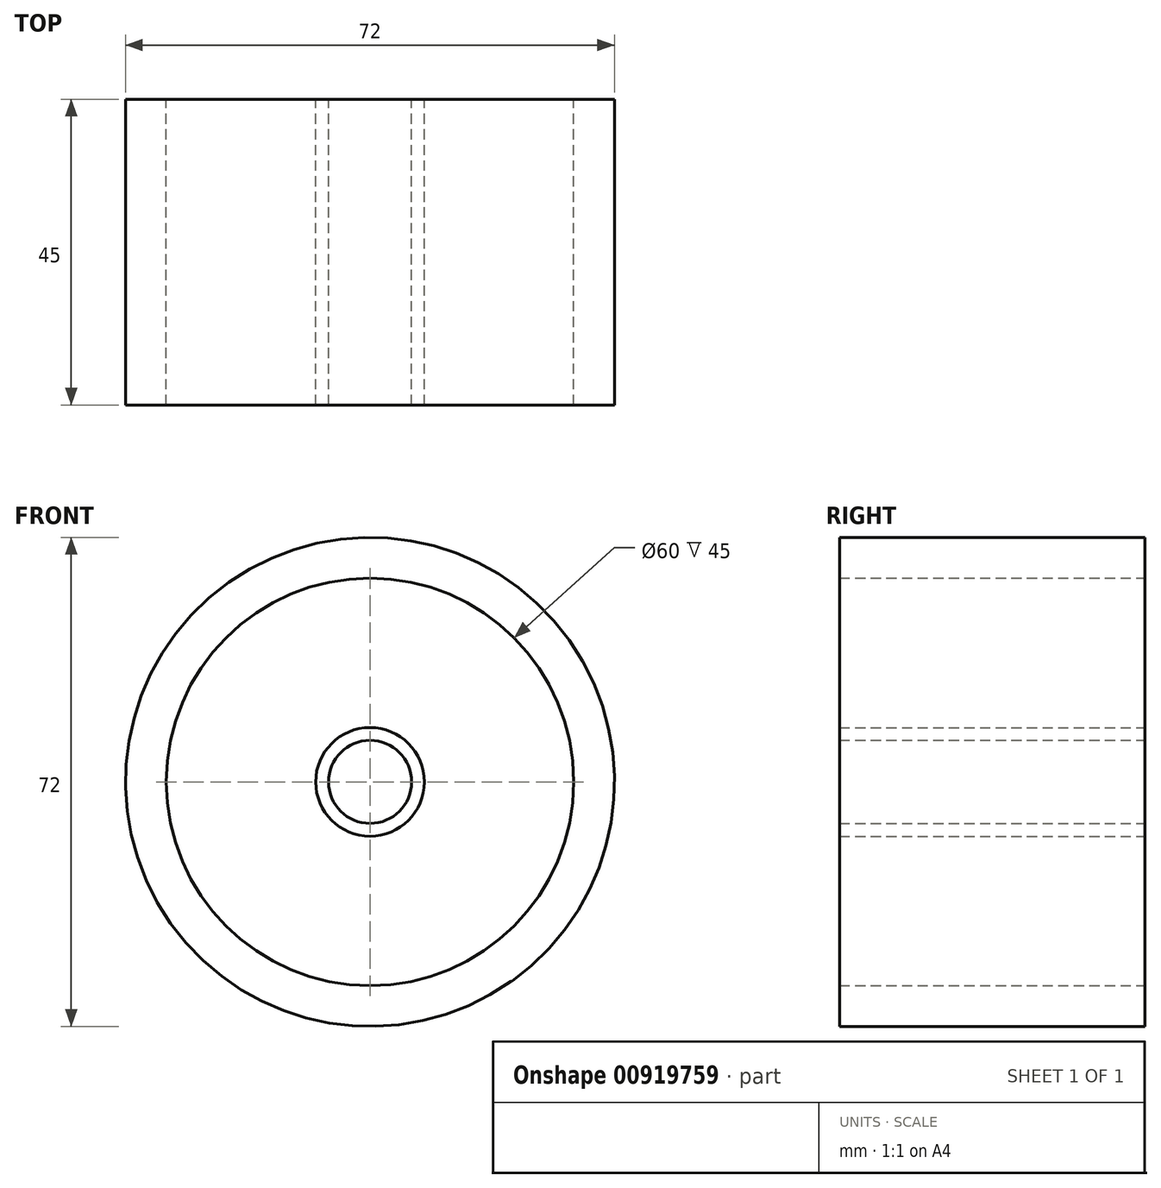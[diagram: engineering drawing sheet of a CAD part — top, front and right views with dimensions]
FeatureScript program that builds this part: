
annotation { "Feature Type Name" : "Feature", "Feature Type Description" : "" }
export const myFeature = defineFeature(function(context is Context, id is Id, definition is map)
    precondition{}
    {
        {
            var Q0;
            Q0=qCreatedBy(makeId("Front.planeOp"),FACE);
            var sketch = newSketch(context, id + "F0", { "sketchPlane" : qUnion([Q0])});
            skCircle(sketch, "E0", {"center": v(0, 0) * mm, "radius": 8 * mm});
            skLineSegment(sketch, "E1.0", {"start": v(-335.4, -14.59) * mm, "end": v(-335.4, -164.59) * mm});
            skCircle(sketch, "E2.0", {"center": v(0, 0) * mm, "radius": 6.12 * mm});
            skCircle(sketch, "E3", {"center": v(0, 0) * mm, "radius": 30 * mm});
            skCircle(sketch, "E4.0", {"center": v(0, 0) * mm, "radius": 36 * mm});
            skFitSpline(sketch, "E5", {"points": [v(-752.9, -15.16) * mm, v(-700, -10.98) * mm, v(-659.23, -24.07) * mm, v(-335.4, -164.59) * mm, v(17.4, -24.44) * mm], "startDerivative": vector(415.77, 48.15) * mm, "endDerivative": vector(894.71, 636.72) * mm});
            skFitSpline(sketch, "E6.0", {"points": [v(-752.21, -21.12) * mm, v(-747.88, -20.62) * mm, v(-741.4, -19.87) * mm, v(-732.98, -18.95) * mm, v(-726.81, -18.34) * mm, v(-720.84, -17.8) * mm, v(-716.06, -17.45) * mm, v(-712.38, -17.23) * mm, v(-709.7, -17.1) * mm, v(-707.1, -17.01) * mm, v(-704.6, -16.96) * mm, v(-702.59, -16.95) * mm, v(-701.04, -16.96) * mm, v(-699.9, -16.99) * mm, v(-698.79, -17.02) * mm, v(-697.35, -17.08) * mm, v(-695.61, -17.19) * mm, v(-693.6, -17.38) * mm, v(-691, -17.71) * mm, v(-688.43, -18.2) * mm, v(-685.78, -18.86) * mm, v(-683.73, -19.47) * mm, v(-681.58, -20.19) * mm, v(-678.56, -21.31) * mm, v(-674.43, -23.07) * mm, v(-669.7, -25.36) * mm, v(-665.45, -27.54) * mm, v(-662.04, -29.37) * mm, v(-658.36, -31.39) * mm, v(-653.12, -34.33) * mm, v(-645.96, -38.44) * mm, v(-636.46, -43.99) * mm, v(-626.1, -50.09) * mm, v(-614.96, -56.65) * mm, v(-603.07, -63.6) * mm, v(-590.49, -70.88) * mm, v(-577.28, -78.4) * mm, v(-558.88, -88.66) * mm, v(-534.54, -101.72) * mm, v(-503.62, -117.2) * mm, v(-471.37, -131.9) * mm, v(-443.73, -143) * mm, v(-421.35, -150.9) * mm, v(-404.48, -156.27) * mm, v(-387.58, -161) * mm, v(-373.5, -164.34) * mm, v(-362.27, -166.62) * mm, v(-353.87, -168.12) * mm, v(-346.89, -169.2) * mm, v(-341.32, -169.94) * mm, v(-337.16, -170.44) * mm, v(-333, -170.88) * mm, v(-327.48, -171.4) * mm, v(-320.6, -171.88) * mm, v(-312.4, -172.24) * mm, v(-301.53, -172.42) * mm, v(-288.05, -172.1) * mm, v(-272.07, -170.86) * mm, v(-256.26, -168.82) * mm, v(-235.41, -165.09) * mm, v(-209.76, -158.6) * mm, v(-179.59, -148.25) * mm, v(-149.94, -135.62) * mm, v(-120.75, -121.03) * mm, v(-91.95, -104.8) * mm, v(-63.46, -87.21) * mm, v(-25.79, -62.36) * mm, v(2.22, -42.6) * mm, v(20.87, -29.33) * mm]});
            skLineSegment(sketch, "E7", {"start": v(-752.9, -15.16) * mm, "end": v(-752.21, -21.12) * mm});
            skSolve(sketch);
        }
        {
            var Q0;
            {var subQ0=sQuery(id+"F0.wireOp",EDGE,"E6.0");Q0=makeQuery(id+"F0.imprint","IMPRINT",FACE,{"disambiguationData":[TD([[makeQuery(id+"F0.imprint","IMPRINT",EDGE,{"derivedFrom":subQ0}),1.0]])]});}
            var Q1;
            {var subQ0=sQuery(id+"F0.wireOp",EDGE,"E3");var subQ1=makeQuery(id+"F0.imprint","IMPRINT",VERTEX,{"disambiguationData":[OD(0.0)],"derivedFrom":subQ0});Q1=makeQuery(id+"F0.imprint","IMPRINT",FACE,{"disambiguationData":[TD([[makeQuery(id+"F0.imprint","IMPRINT",EDGE,{"disambiguationData":[TD([[subQ1,-1.0]])],"derivedFrom":subQ0}),-1.0]])]});}
            var Q2;
            Q2=makeQuery(id+"F0.imprint","IMPRINT",FACE,{"disambiguationData":[TD([[makeQuery(id+"F0.imprint","IMPRINT",EDGE,{"derivedFrom":sQuery(id+"F0.wireOp",EDGE,"E0")}),1.0]])]});
            extrude(context, id + "F1", {"entities" : qUnion([Q0, Q1, Q2]), "depth" : 45 * mm, "offsetDistance" : 25 * mm});
        }
    });
